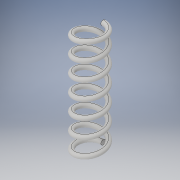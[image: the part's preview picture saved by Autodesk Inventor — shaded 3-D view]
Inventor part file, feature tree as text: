
AUTODESK INVENTOR PART (.ipt)
format: ipt  version: 2019 (Build 230136000, 136)  size: 446,464 bytes
history: native  units: in
note: dims shown in document units (in); Inventor stores cm internally (conversion verified against a paired STEP export)
features: helix x1, sketch x1
ambient origin geometry x8: Origin, YZ Plane, XZ Plane, XY Plane, X Axis, Y Axis, Z Axis, Center Point
bodies: Solid1 (feature_tree)
feature tree (2):
  helix  "Coil1"  [1 undecoded]
  sketch  "Sketch1"  dims[d1=0.0984in d2=1.7717in d3=0.3937in d4=2.1654in d5=2.3622in d6=0.0in d7=90.0deg d8=90.0deg d9=90.0deg d10=90.0deg]
note: 1 required parameter value undecoded (feature->parameter linkage not recoverable at this tier; creation-order binding heuristic only, values carry confidence <= 0.55)
